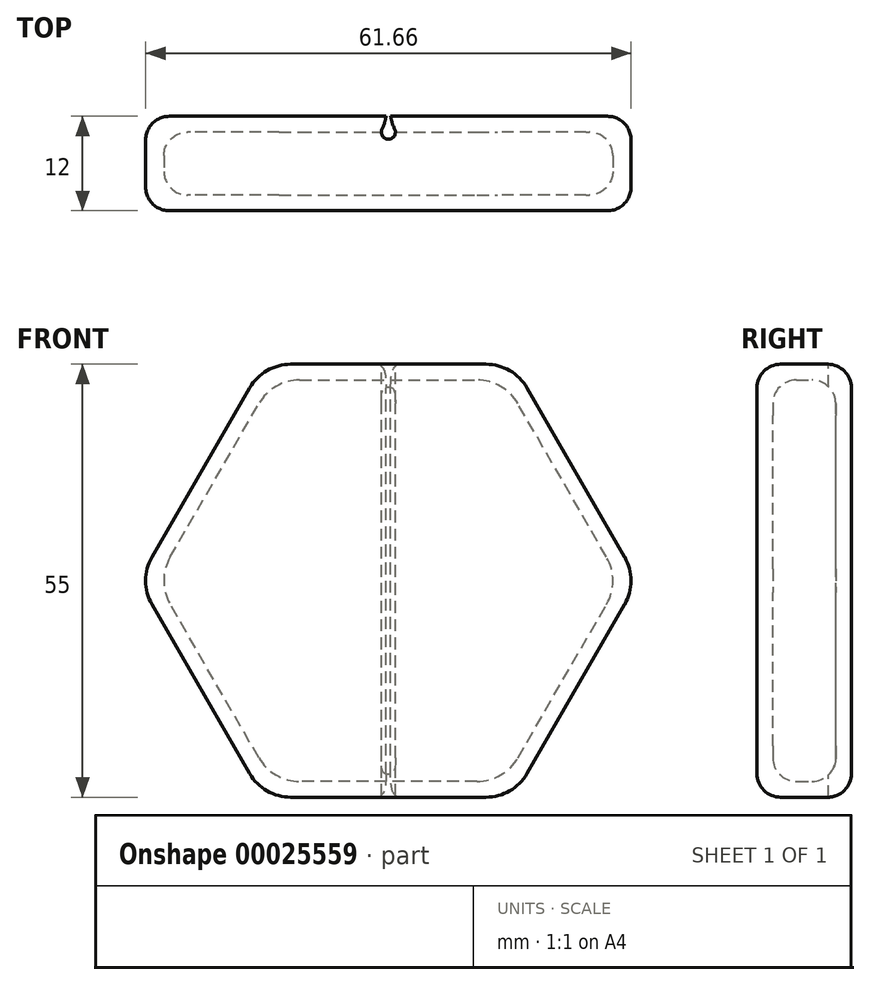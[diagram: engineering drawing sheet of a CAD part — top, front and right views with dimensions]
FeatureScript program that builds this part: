
annotation { "Feature Type Name" : "Feature", "Feature Type Description" : "" }
export const myFeature = defineFeature(function(context is Context, id is Id, definition is map)
    precondition{}
    {
        {
            var Q0;
            Q0=qCreatedBy(makeId("Front.planeOp"),FACE);
            var sketch = newSketch(context, id + "F0", { "sketchPlane" : qUnion([Q0])});
            skCircle(sketch, "E0.cCircle", {"center": v(0, 0) * mm, "radius": 27.5 * mm, "construction": true});
            skLineSegment(sketch, "E0.0", {"start": v(-15.88, 27.5) * mm, "end": v(0, 27.5) * mm});
            skLineSegment(sketch, "E0.3", {"start": v(0, -27.5) * mm, "end": v(-15.88, -27.5) * mm});
            skLineSegment(sketch, "E0.4", {"start": v(-15.88, -27.5) * mm, "end": v(-31.75, 0) * mm});
            skLineSegment(sketch, "E0.5", {"start": v(-31.75, 0) * mm, "end": v(-15.88, 27.5) * mm});
            skPoint(sketch, "E0.0.midPoint", {"position": v(0, 27.5) * mm});
            skLineSegment(sketch, "E1", {"start": v(0, 27.5) * mm, "end": v(0, -27.5) * mm});
            skPoint(sketch, "E2.orphan", {"position": v(15.88, 27.5) * mm});
            skPoint(sketch, "E3.orphan", {"position": v(31.75, 0) * mm});
            skPoint(sketch, "E4.orphan", {"position": v(15.88, -27.5) * mm});
            skSolve(sketch);
        }
        {
            var Q0;
            Q0 = qSketchRegion(id + "F0", true);
            extrude(context, id + "F1", {"entities" : qUnion([Q0]), "depth" : 12 * mm});
        }
        {
            var Q0;
            Q0 = qSketchRegion(id + "F0", true);
            extrude(context, id + "F2", {"entities" : qUnion([Q0]), "depth" : 12 * mm});
        }
        {
            var Q0;
            Q0=makeQuery(id+"F2.opExtrude","SWEPT_BODY",BODY,{"disambiguationData":[OSD([sQuery(id+"F0.wireOp",EDGE,"E0.0"),sQuery(id+"F0.wireOp",EDGE,"E0.3"),sQuery(id+"F0.wireOp",EDGE,"E0.4"),sQuery(id+"F0.wireOp",EDGE,"E0.5"),sQuery(id+"F0.wireOp",EDGE,"E1")])]});
            deleteBodies(context, id + "F3", {"entities" : qUnion([Q0])});
        }
        {
            var Q0;
            Q0=makeQuery(id+"F1.opExtrude","SWEPT_FACE",FACE,{"disambiguationData":[OSD([sQuery(id+"F0.wireOp",EDGE,"E1")])]});
            shell(context, id + "F4", {"entities" : qUnion([Q0]), "thickness" : 2 * mm});
        }
        {
            var Q0;
            Q0=makeQuery(id+"F4.opShell","OFFSET_EDGE",EDGE,{"disambiguationData":[OSD([sQuery(id+"F0.wireOp",EDGE,"E0.3"),sQuery(id+"F0.wireOp",EDGE,"E0.4")])]});
            var Q1;
            Q1=makeQuery(id+"F4.opShell","OFFSET_EDGE",EDGE,{"disambiguationData":[OSD([sQuery(id+"F0.wireOp",EDGE,"E0.4"),sQuery(id+"F0.wireOp",EDGE,"E0.5")])]});
            var Q2;
            Q2=makeQuery(id+"F4.opShell","OFFSET_EDGE",EDGE,{"disambiguationData":[OSD([sQuery(id+"F0.wireOp",EDGE,"E0.0"),sQuery(id+"F0.wireOp",EDGE,"E0.5")])]});
            var Q3;
            Q3=makeQuery(id+"F1.opExtrude","SWEPT_EDGE",EDGE,{"disambiguationData":[OSD([sQuery(id+"F0.wireOp",EDGE,"E0.3"),sQuery(id+"F0.wireOp",EDGE,"E0.4")])]});
            var Q4;
            Q4=makeQuery(id+"F1.opExtrude","SWEPT_EDGE",EDGE,{"disambiguationData":[OSD([sQuery(id+"F0.wireOp",EDGE,"E0.0"),sQuery(id+"F0.wireOp",EDGE,"E0.5")])]});
            var Q5;
            Q5=makeQuery(id+"F1.opExtrude","SWEPT_EDGE",EDGE,{"disambiguationData":[OSD([sQuery(id+"F0.wireOp",EDGE,"E0.4"),sQuery(id+"F0.wireOp",EDGE,"E0.5")])]});
            fillet(context, id + "F5", {"entities" : qUnion([Q0, Q1, Q2, Q3, Q4, Q5]), "radius" : 6 * mm, "tangentPropagation" : true, "allowEdgeOverflow" : false});
        }
        {
            var Q0;
            {var subQ0=sQuery(id+"F0.wireOp",EDGE,"E0.3");Q0=makeQuery(id+"F4.opShell","OFFSET_EDGE",EDGE,{"disambiguationData":[OSD([subQ0]),TDD([makeQuery(id+"F1.opExtrude","CAP_EDGE",EDGE,{"disambiguationData":[OSD([subQ0])],"isStart":true})])]});}
            var Q1;
            {var subQ0=sQuery(id+"F0.wireOp",EDGE,"E0.5");Q1=makeQuery(id+"F4.opShell","OFFSET_EDGE",EDGE,{"disambiguationData":[OSD([subQ0]),TDD([makeQuery(id+"F1.opExtrude","CAP_EDGE",EDGE,{"disambiguationData":[OSD([subQ0])],"isStart":false})])]});}
            var Q2;
            Q2=makeQuery(id+"F1.opExtrude","CAP_EDGE",EDGE,{"disambiguationData":[OSD([sQuery(id+"F0.wireOp",EDGE,"E0.0")])],"isStart":true});
            var Q3;
            Q3=makeQuery(id+"F1.opExtrude","CAP_EDGE",EDGE,{"disambiguationData":[OSD([sQuery(id+"F0.wireOp",EDGE,"E0.0")])],"isStart":false});
            fillet(context, id + "F6", {"entities" : qUnion([Q0, Q1, Q2, Q3]), "radius" : 3 * mm, "tangentPropagation" : true, "allowEdgeOverflow" : false});
        }
        {
            var Q0;
            Q0=makeQuery(id+"F1.opExtrude","CAP_FACE",FACE,{"disambiguationData":[OSD([sQuery(id+"F0.wireOp",EDGE,"E0.0"),sQuery(id+"F0.wireOp",EDGE,"E0.3"),sQuery(id+"F0.wireOp",EDGE,"E0.4"),sQuery(id+"F0.wireOp",EDGE,"E0.5"),sQuery(id+"F0.wireOp",EDGE,"E1")])],"isStart":true});
            var sketch = newSketch(context, id + "F7", { "sketchPlane" : qUnion([Q0])});
            skLineSegment(sketch, "E5.rect.bottom", {"start": v(-0.3, -27.6) * mm, "end": v(0.3, -27.6) * mm});
            skLineSegment(sketch, "E5.rect.top", {"start": v(-0.3, 27.6) * mm, "end": v(0.3, 27.6) * mm});
            skLineSegment(sketch, "E5.rect.left", {"start": v(-0.3, -27.6) * mm, "end": v(-0.3, 27.6) * mm});
            skLineSegment(sketch, "E5.rect.right", {"start": v(0.3, -27.6) * mm, "end": v(0.3, 27.6) * mm});
            skPoint(sketch, "E5.rect.middle", {"position": v(0, 0) * mm});
            skSolve(sketch);
        }
        {
            var Q0;
            Q0 = qSketchRegion(id + "F7", true);
            extrude(context, id + "F8", {"entities" : qUnion([Q0]), "operationType" : NewBodyOperationType.REMOVE, "oppositeDirection" : true, "depth" : 2 * mm});
        }
        {
            var Q0;
            Q0=makeQuery(id+"F1.opExtrude","SWEPT_BODY",BODY,{"disambiguationData":[OSD([sQuery(id+"F0.wireOp",EDGE,"E0.0"),sQuery(id+"F0.wireOp",EDGE,"E0.3"),sQuery(id+"F0.wireOp",EDGE,"E0.4"),sQuery(id+"F0.wireOp",EDGE,"E0.5"),sQuery(id+"F0.wireOp",EDGE,"E1")])]});
            var Q1;
            Q1=makeQuery(id+"F1.opExtrude","SWEPT_FACE",FACE,{"disambiguationData":[OSD([sQuery(id+"F0.wireOp",EDGE,"E1")])]});
            mirror(context, id + "F9", {"operationType" : NewBodyOperationType.ADD, "entities" : qUnion([Q0]), "mirrorPlane" : qUnion([Q1])});
        }
        {
            var Q0;
            {var subQ0=makeQuery(id+"F1.opExtrude","SWEPT_FACE",FACE,{"disambiguationData":[OSD([sQuery(id+"F0.wireOp",EDGE,"E0.0")])]});Q0=makeQuery(id+"F9.boolean.opBoolean","MERGE",FACE,{"derivedFrom":[subQ0,makeQuery(id+"F9.opPattern","COPY",FACE,{"derivedFrom":subQ0,"instanceName":"1"})]});}
            var sketch = newSketch(context, id + "F10", { "sketchPlane" : qUnion([Q0])});
            skCircle(sketch, "E6", {"center": v(0, -2) * mm, "radius": 0.9 * mm});
            skSolve(sketch);
        }
        {
            var Q0;
            Q0 = qSketchRegion(id + "F10", true);
            extrude(context, id + "F11", {"entities" : qUnion([Q0]), "operationType" : NewBodyOperationType.REMOVE, "endBound" : BoundingType.THROUGH_ALL, "oppositeDirection" : true, "depth" : 25 * mm});
        }
        {
            var Q0;
            Q0=makeQuery(id+"F11.boolean.opBoolean","INTERSECT",EDGE,{"disambiguationData":[OD(0.0)],"derivedFrom":[makeQuery(id+"F8.boolean.opBoolean","COPY",FACE,{"derivedFrom":makeQuery(id+"F8.opExtrude","SWEPT_FACE",FACE,{"disambiguationData":[OSD([sQuery(id+"F7.wireOp",EDGE,"E5.rect.right")])]})}),makeQuery(id+"F11.opExtrude","SWEPT_FACE",FACE,{"disambiguationData":[OSD([sQuery(id+"F10.wireOp",EDGE,"E6")])]})]});
            var Q1;
            Q1=makeQuery(id+"F11.boolean.opBoolean","INTERSECT",EDGE,{"disambiguationData":[OD(0.0)],"derivedFrom":[makeQuery(id+"F9.opPattern","COPY",FACE,{"derivedFrom":makeQuery(id+"F8.boolean.opBoolean","COPY",FACE,{"derivedFrom":makeQuery(id+"F8.opExtrude","SWEPT_FACE",FACE,{"disambiguationData":[OSD([sQuery(id+"F7.wireOp",EDGE,"E5.rect.right")])]})}),"instanceName":"1"}),makeQuery(id+"F11.opExtrude","SWEPT_FACE",FACE,{"disambiguationData":[OSD([sQuery(id+"F10.wireOp",EDGE,"E6")])]})]});
            fillet(context, id + "F12", {"entities" : qUnion([Q0, Q1]), "radius" : 5 * mm, "tangentPropagation" : true, "allowEdgeOverflow" : false});
        }
    });
